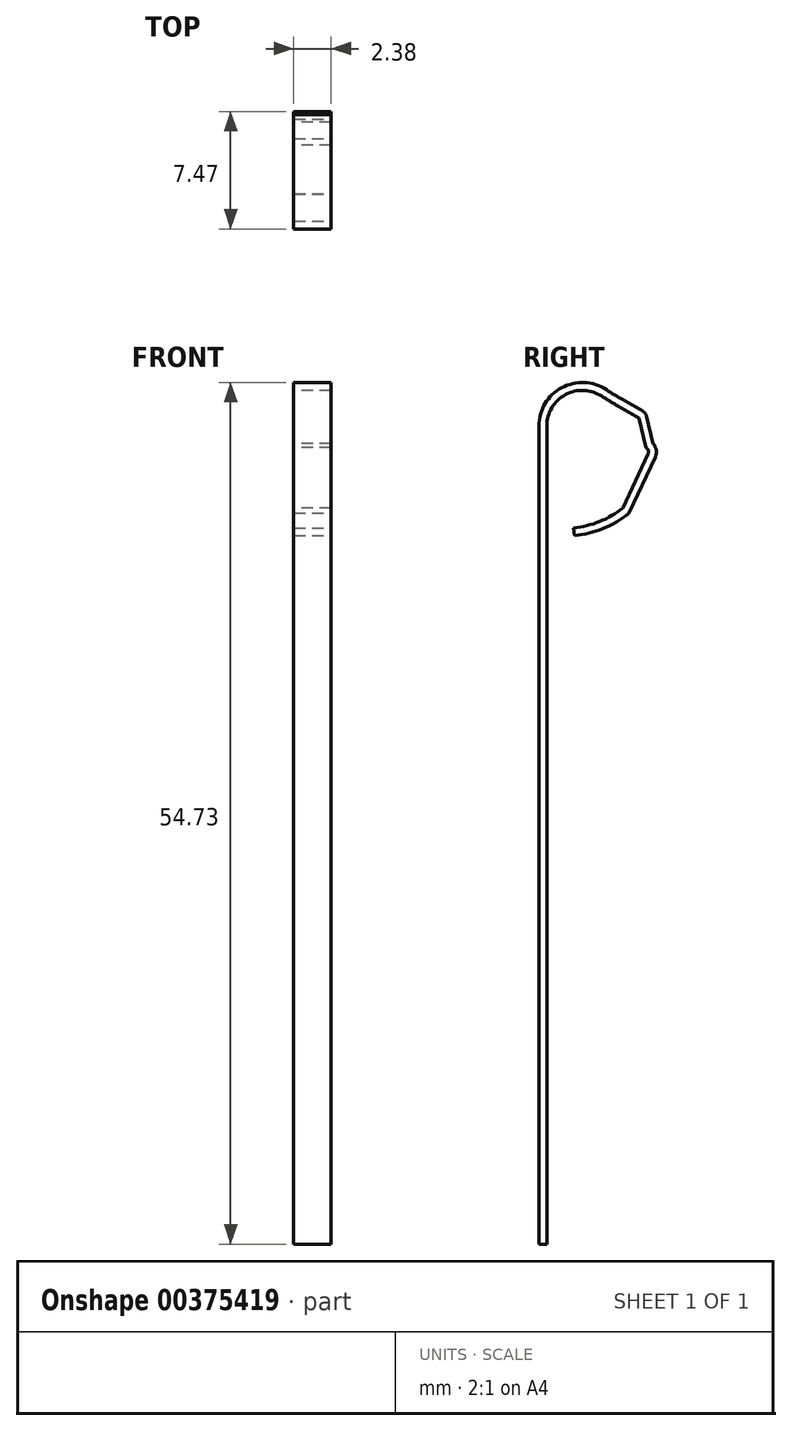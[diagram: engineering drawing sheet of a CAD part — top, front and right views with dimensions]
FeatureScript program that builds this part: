
annotation { "Feature Type Name" : "Feature", "Feature Type Description" : "" }
export const myFeature = defineFeature(function(context is Context, id is Id, definition is map)
    precondition{}
    {
        {
            var Q0;
            Q0=qCreatedBy(makeId("Top.planeOp"),FACE);
            var sketch = newSketch(context, id + "F0", { "sketchPlane" : qUnion([Q0])});
            skLineSegment(sketch, "E0.bottom", {"start": v(-1.2, 0.25) * mm, "end": v(1.2, 0.25) * mm});
            skLineSegment(sketch, "E0.top", {"start": v(-1.2, -0.25) * mm, "end": v(1.2, -0.25) * mm});
            skLineSegment(sketch, "E0.left", {"start": v(-1.2, 0.25) * mm, "end": v(-1.2, -0.25) * mm});
            skLineSegment(sketch, "E0.right", {"start": v(1.2, 0.25) * mm, "end": v(1.2, -0.25) * mm});
            skPoint(sketch, "E0.middle", {"position": v(0, 0) * mm});
            skSolve(sketch);
        }
        {
            var Q0;
            Q0=qCreatedBy(makeId("Right.planeOp"),FACE);
            var sketch = newSketch(context, id + "F1", { "sketchPlane" : qUnion([Q0])});
            skLineSegment(sketch, "E1", {"start": v(0, 0) * mm, "end": v(0, 19.05) * mm});
            skLineSegment(sketch, "E2", {"start": v(0, 19.05) * mm, "end": v(0, 47.31) * mm});
            skLineSegment(sketch, "E3", {"start": v(0, 47.31) * mm, "end": v(0, 51.97) * mm});
            skArc(sketch, "E4", {"start": v(3.9, 54.07) * mm, "mid": v(1.32, 54.18) * mm, "end": v(0, 51.97) * mm});
            skArc(sketch, "E5", {"start": v(1.98, 45.25) * mm, "mid": v(3.73, 45.68) * mm, "end": v(5.28, 46.6) * mm});
            skLineSegment(sketch, "E6", {"start": v(6.91, 50.1) * mm, "end": v(5.28, 46.6) * mm});
            skPoint(sketch, "E7.visualSharp", {"position": v(7.07, 50.42) * mm});
            skArc(sketch, "E7.filletArc", {"start": v(6.91, 50.1) * mm, "mid": v(6.95, 50.44) * mm, "end": v(6.78, 50.73) * mm});
            skLineSegment(sketch, "E8", {"start": v(4.89, 53.46) * mm, "end": v(6.22, 52.7) * mm});
            skLineSegment(sketch, "E9", {"start": v(6.35, 52.53) * mm, "end": v(6.78, 50.73) * mm});
            skPoint(sketch, "E10.visualSharp", {"position": v(4.13, 53.89) * mm});
            skArc(sketch, "E10.filletArc", {"start": v(3.9, 54.07) * mm, "mid": v(4.39, 53.75) * mm, "end": v(4.89, 53.46) * mm});
            skPoint(sketch, "E11.visualSharp", {"position": v(6.32, 52.64) * mm});
            skArc(sketch, "E11.filletArc", {"start": v(6.35, 52.53) * mm, "mid": v(6.3, 52.62) * mm, "end": v(6.22, 52.7) * mm});
            skSolve(sketch);
        }
        {
            var Q0;
            Q0=qSketchRegion(id+"F0",true);
            var Q1;
            Q1=qConstructionFilter(qBodyType(qCreatedBy(id+"F1",EDGE),BodyType.WIRE),ConstructionObject.NO);
            sweep(context, id + "F2", {"profiles" : qUnion([Q0]), "path" : qUnion([Q1])});
        }
    });
